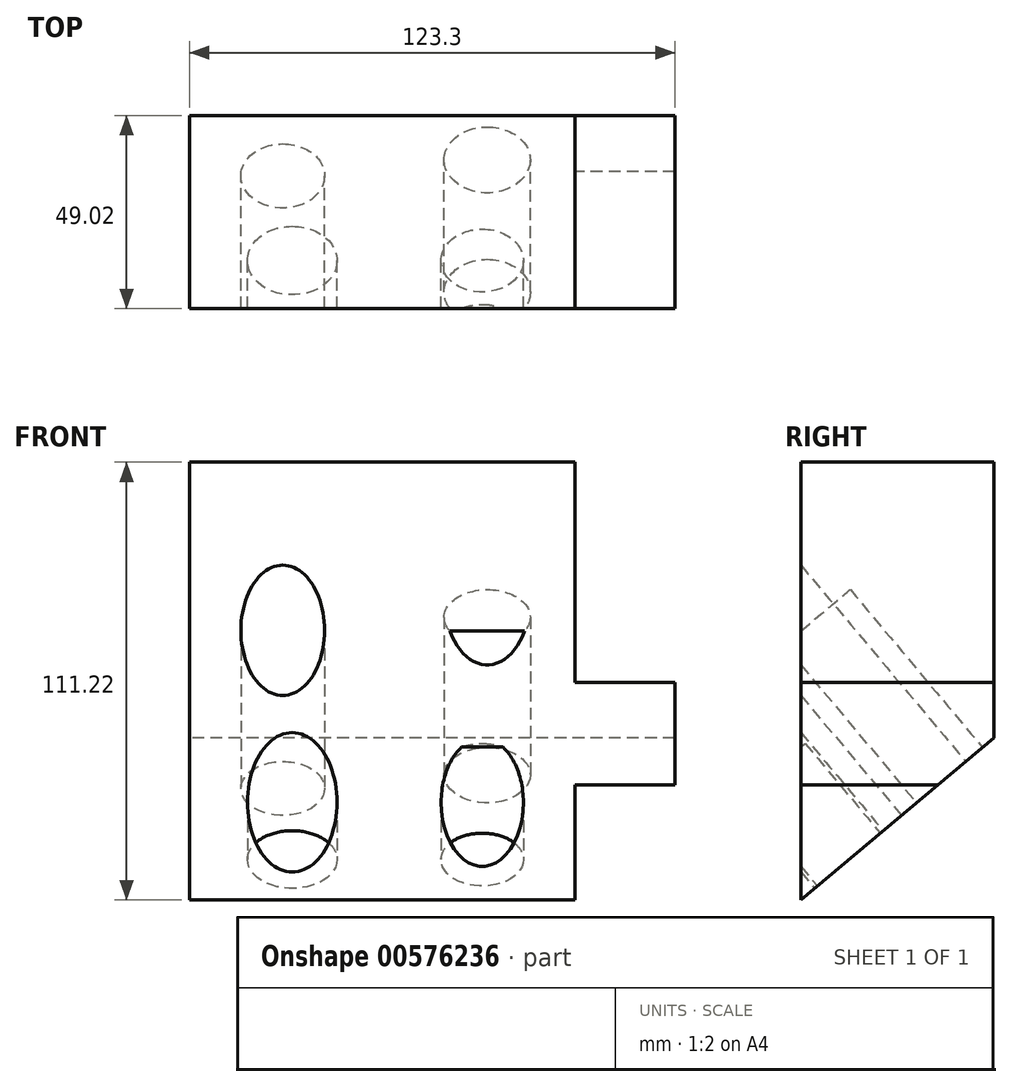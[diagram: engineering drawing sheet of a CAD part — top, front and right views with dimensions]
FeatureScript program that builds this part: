
annotation { "Feature Type Name" : "Feature", "Feature Type Description" : "" }
export const myFeature = defineFeature(function(context is Context, id is Id, definition is map)
    precondition{}
    {
        {
            var Q0;
            Q0=qCreatedBy(makeId("Front.planeOp"),FACE);
            var sketch = newSketch(context, id + "F0", { "sketchPlane" : qUnion([Q0])});
            skLineSegment(sketch, "E0.bottom", {"start": v(48.95, 55.95) * mm, "end": v(-48.95, 55.95) * mm});
            skLineSegment(sketch, "E0.top", {"start": v(48.95, -55.95) * mm, "end": v(-48.95, -55.95) * mm});
            skLineSegment(sketch, "E0.left", {"start": v(48.95, 55.95) * mm, "end": v(48.95, -55.95) * mm});
            skLineSegment(sketch, "E0.right", {"start": v(-48.95, 55.95) * mm, "end": v(-48.95, -55.95) * mm});
            skPoint(sketch, "E0.middle", {"position": v(0, 0) * mm});
            skSolve(sketch);
        }
        {
            var Q0;
            Q0=makeQuery(id+"F0.imprint","IMPRINT",FACE,{"disambiguationData":[TD([[makeQuery(id+"F0.imprint","IMPRINT",EDGE,{"derivedFrom":sQuery(id+"F0.wireOp",EDGE,"E0.bottom")}),1.0]])]});
            extrude(context, id + "F1", {"entities" : qUnion([Q0]), "oppositeDirection" : true, "depth" : 49.02 * mm, "offsetDistance" : 25.4 * mm});
        }
        {
            var Q0;
            Q0=makeQuery(id+"F1.opExtrude","CAP_FACE",FACE,{"disambiguationData":[OSD([sQuery(id+"F0.wireOp",EDGE,"E0.bottom"),sQuery(id+"F0.wireOp",EDGE,"E0.top"),sQuery(id+"F0.wireOp",EDGE,"E0.left"),sQuery(id+"F0.wireOp",EDGE,"E0.right")])],"isStart":false});
            var sketch = newSketch(context, id + "F2", { "sketchPlane" : qUnion([Q0])});
            skLineSegment(sketch, "E1", {"start": v(-48.95, -14.13) * mm, "end": v(48.95, -14.13) * mm});
            skSolve(sketch);
        }
        {
            var Q0;
            Q0=sQuery(id+"F2.wireOp",EDGE,"E1");
            cPlane(context, id + "F3", {"entities" : qUnion([Q0]), "cplaneType" : CPlaneType.LINE_ANGLE, "offset" : 25.4 * mm, "angle" : 50 * degree, "width" : 152.4 * mm, "height" : 152.4 * mm});
        }
        {
            var Q0;
            {var subQ0=sQuery(id+"F2.wireOp",EDGE,"E1");Q0=makeQuery(id+"F2.imprint","IMPRINT",FACE,{"disambiguationData":[TD([[makeQuery(id+"F2.imprint","IMPRINT",EDGE,{"derivedFrom":subQ0}),-1.0]])]});}
            var Q1;
            Q1=qCreatedBy(id+"F3.planeOp",FACE);
            extrude(context, id + "F4", {"entities" : qUnion([Q0]), "operationType" : NewBodyOperationType.REMOVE, "endBound" : BoundingType.UP_TO_SURFACE, "oppositeDirection" : true, "depth" : 25.4 * mm, "endBoundEntityFace" : qUnion([Q1]), "offsetDistance" : 25.4 * mm});
        }
        {
            var Q0;
            Q0=makeQuery(id+"F4.boolean.opBoolean","COPY",FACE,{"derivedFrom":makeQuery(id+"F4.opExtrude","CAP_FACE",FACE,{"disambiguationData":[OSD([sQuery(id+"F0.wireOp",EDGE,"E0.top"),sQuery(id+"F0.wireOp",EDGE,"E0.left"),sQuery(id+"F0.wireOp",EDGE,"E0.right"),sQuery(id+"F2.wireOp",EDGE,"E1")])],"isStart":false})});
            var sketch = newSketch(context, id + "F5", { "sketchPlane" : qUnion([Q0])});
            skCircle(sketch, "E2", {"center": v(26.67, -13.79) * mm, "radius": 10.95 * mm});
            skCircle(sketch, "E3", {"center": v(31.56, 16.57) * mm, "radius": 11.78 * mm});
            skCircle(sketch, "E4", {"center": v(-19.34, 13.78) * mm, "radius": 11.1 * mm});
            skCircle(sketch, "E5", {"center": v(-22.15, -14.34) * mm, "radius": 12.25 * mm});
            skSolve(sketch);
        }
        {
            var Q0;
            Q0=makeQuery(id+"F4.boolean.opBoolean","COPY",FACE,{"derivedFrom":makeQuery(id+"F4.opExtrude","CAP_FACE",FACE,{"disambiguationData":[OSD([sQuery(id+"F0.wireOp",EDGE,"E0.top"),sQuery(id+"F0.wireOp",EDGE,"E0.left"),sQuery(id+"F0.wireOp",EDGE,"E0.right"),sQuery(id+"F2.wireOp",EDGE,"E1")])],"isStart":false})});
            var sketch = newSketch(context, id + "F6", { "sketchPlane" : qUnion([Q0])});
            skCircle(sketch, "E6", {"center": v(25.4, 19.61) * mm, "radius": 10.44 * mm});
            skSolve(sketch);
        }
        {
            var Q0;
            Q0=makeQuery(id+"F4.boolean.opBoolean","COPY",FACE,{"derivedFrom":makeQuery(id+"F4.opExtrude","CAP_FACE",FACE,{"disambiguationData":[OSD([sQuery(id+"F0.wireOp",EDGE,"E0.top"),sQuery(id+"F0.wireOp",EDGE,"E0.left"),sQuery(id+"F0.wireOp",EDGE,"E0.right"),sQuery(id+"F2.wireOp",EDGE,"E1")])],"isStart":false})});
            var sketch = newSketch(context, id + "F7", { "sketchPlane" : qUnion([Q0])});
            skCircle(sketch, "E7", {"center": v(-25.28, -8.49) * mm, "radius": 10.64 * mm});
            skSolve(sketch);
        }
        {
            var Q0;
            Q0=makeQuery(id+"F4.boolean.opBoolean","COPY",FACE,{"derivedFrom":makeQuery(id+"F4.opExtrude","CAP_FACE",FACE,{"disambiguationData":[OSD([sQuery(id+"F0.wireOp",EDGE,"E0.top"),sQuery(id+"F0.wireOp",EDGE,"E0.left"),sQuery(id+"F0.wireOp",EDGE,"E0.right"),sQuery(id+"F2.wireOp",EDGE,"E1")])],"isStart":false})});
            var sketch = newSketch(context, id + "F8", { "sketchPlane" : qUnion([Q0])});
            skCircle(sketch, "E8", {"center": v(-22.88, 19.6) * mm, "radius": 11.38 * mm});
            skSolve(sketch);
        }
        {
            var Q0;
            Q0=makeQuery(id+"F5.imprint","IMPRINT",FACE,{"disambiguationData":[TD([[makeQuery(id+"F5.imprint","IMPRINT",EDGE,{"derivedFrom":sQuery(id+"F5.wireOp",EDGE,"E2")}),1.0]])]});
            extrude(context, id + "F9", {"entities" : qUnion([Q0]), "operationType" : NewBodyOperationType.REMOVE, "oppositeDirection" : true, "depth" : 52.32 * mm, "offsetDistance" : 25.4 * mm});
        }
        {
            var Q0;
            Q0 = qSketchRegion(id + "F6", true);
            extrude(context, id + "F10", {"entities" : qUnion([Q0]), "operationType" : NewBodyOperationType.REMOVE, "oppositeDirection" : true, "depth" : 29.72 * mm, "offsetDistance" : 25.4 * mm});
        }
        {
            var Q0;
            Q0 = qSketchRegion(id + "F7", true);
            extrude(context, id + "F11", {"entities" : qUnion([Q0]), "operationType" : NewBodyOperationType.REMOVE, "oppositeDirection" : true, "depth" : 212.34 * mm, "offsetDistance" : 25.4 * mm});
        }
        {
            var Q0;
            Q0 = qSketchRegion(id + "F8", true);
            extrude(context, id + "F12", {"entities" : qUnion([Q0]), "operationType" : NewBodyOperationType.REMOVE, "oppositeDirection" : true, "depth" : 73.4 * mm, "offsetDistance" : 25.4 * mm});
        }
        {
            var Q0;
            Q0=makeQuery(id+"F1.opExtrude","SWEPT_FACE",FACE,{"disambiguationData":[OSD([sQuery(id+"F0.wireOp",EDGE,"E0.left")])]});
            var sketch = newSketch(context, id + "F13", { "sketchPlane" : qUnion([Q0])});
            skLineSegment(sketch, "E9", {"start": v(49.02, 0) * mm, "end": v(0, 0) * mm});
            skLineSegment(sketch, "E10", {"start": v(0, 0) * mm, "end": v(0, -26) * mm});
            skLineSegment(sketch, "E11", {"start": v(0, -26) * mm, "end": v(34.87, -26) * mm});
            skLineSegment(sketch, "E12", {"start": v(34.87, -26) * mm, "end": v(49.02, -14.13) * mm});
            skLineSegment(sketch, "E13", {"start": v(49.02, -14.13) * mm, "end": v(49.02, 0) * mm});
            skSolve(sketch);
        }
        {
            var Q0;
            Q0=makeQuery(id+"F13.imprint","IMPRINT",FACE,{"disambiguationData":[TD([[makeQuery(id+"F13.imprint","IMPRINT",EDGE,{"derivedFrom":sQuery(id+"F13.wireOp",EDGE,"E9")}),1.0]])]});
            extrude(context, id + "F14", {"entities" : qUnion([Q0]), "operationType" : NewBodyOperationType.ADD, "depth" : 25.4 * mm, "offsetDistance" : 25.4 * mm});
        }
    });
